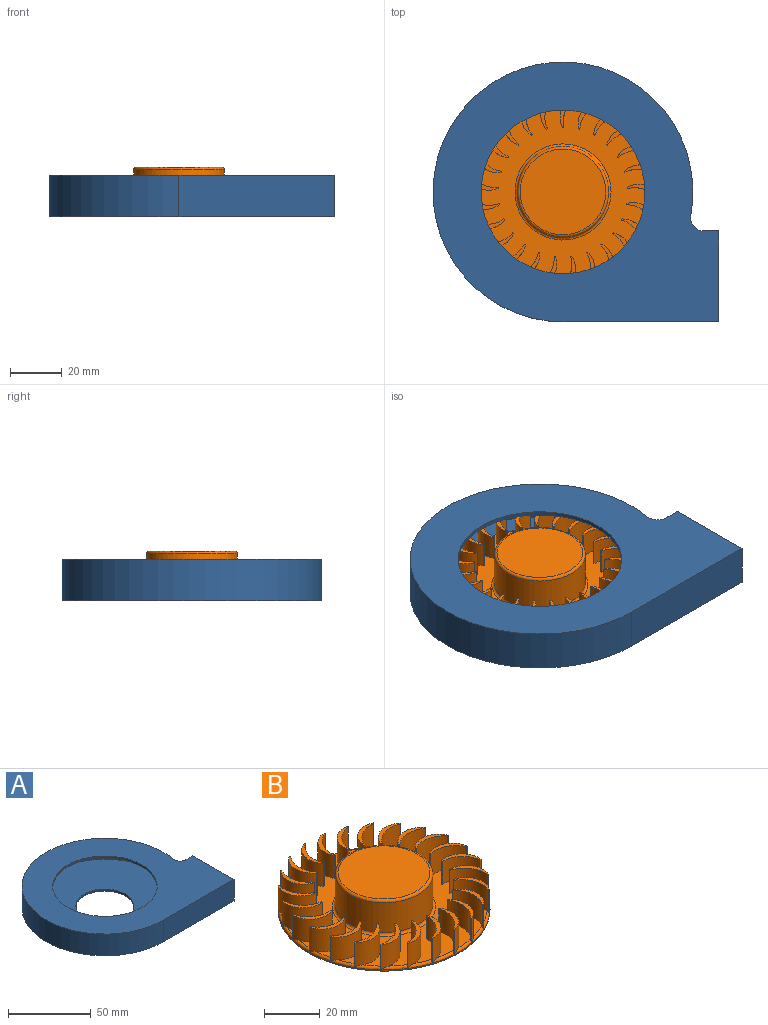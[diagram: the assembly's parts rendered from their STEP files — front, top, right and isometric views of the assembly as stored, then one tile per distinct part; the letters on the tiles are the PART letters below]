
ASSEMBLY  parts=2 mates=1
PART A: 15 faces, bbox 110x100x16 mm
  f0: cylinder r=17.5mm len=35mm, axis (0,0,-1), area 164.9mm2, adj f7,f13
  f1: plane 35x16mm, normal (1,0,0), area 144mm2, adj f2,f5,f6,f7,f8,f11,f12,f13
  f2: plane 16x5.92mm, normal (0,1,0), area 94.7mm2, adj f1,f3,f6,f7
  f3: cylinder r=5mm len=16mm, axis (0,0,-1), area 140.3mm2, adj f2,f4,f6,f7
  f4: cylinder r=50mm len=100mm, axis (0,0,-1), area 3916.2mm2, adj f3,f5,f6,f7
  f5: plane 60x16mm, normal (0,-1,0), area 960mm2, adj f1,f4,f6,f7
  f6: plane 110x100mm, normal (0,0,1), area 5620.7mm2, adj f1,f2,f3,f4,f5,f14
  f7: plane 110x100mm, normal (0,0,-1), area 7775.8mm2, adj f0,f1,f2,f3,f4,f5
  f8: plane 13x5.92mm, normal (0,-1,0), area 76.9mm2, adj f1,f9,f12,f13
  f9: cylinder r=6.5mm len=13mm, axis (0,0,-1), area 148.2mm2, adj f8,f10,f12,f13
  f10: cylinder r=48.5mm len=97mm, axis (0,0,-1), area 3086.4mm2, adj f9,f11,f12,f13
  f11: plane 60x13mm, normal (0,1,0), area 780mm2, adj f1,f10,f12,f13
  f12: plane 108.5x97mm, normal (0,0,-1), area 5145.1mm2, adj f1,f8,f9,f10,f11,f14
  f13: plane 108.5x97mm, normal (0,0,1), area 7300.2mm2, adj f0,f1,f8,f9,f10,f11
  f14: cylinder r=31.5mm len=63mm, axis (0,0,-1), area 296.9mm2, adj f6,f12
PART B: 160 faces, bbox 76.7x76.7x16.5 mm
  f0: torus R=37mm, axis (0,0,1), area 13.3mm2, adj f25,f27,f150,f153,f156
  f1: torus R=37mm, axis (0,0,1), area 13.3mm2, adj f25,f27,f145,f148,f151
  f2: torus R=37mm, axis (0,0,1), area 13.3mm2, adj f25,f27,f140,f143,f146
  f3: torus R=37mm, axis (0,0,1), area 13.3mm2, adj f25,f27,f135,f138,f141
  f4: torus R=37mm, axis (0,0,1), area 13.3mm2, adj f25,f27,f130,f133,f136
  f5: torus R=37mm, axis (0,0,1), area 13.3mm2, adj f25,f27,f125,f128,f131
  f6: torus R=37mm, axis (0,0,1), area 13.3mm2, adj f25,f27,f120,f123,f126
  f7: torus R=37mm, axis (0,0,1), area 13.3mm2, adj f25,f27,f115,f118,f121
  f8: torus R=37mm, axis (0,0,1), area 13.3mm2, adj f25,f27,f110,f113,f116
  f9: torus R=37mm, axis (0,0,1), area 13.3mm2, adj f25,f27,f105,f108,f111
  f10: torus R=37mm, axis (0,0,1), area 13.3mm2, adj f25,f27,f100,f103,f106
  f11: torus R=37mm, axis (0,0,1), area 13.3mm2, adj f25,f27,f95,f98,f101
  f12: torus R=37mm, axis (0,0,1), area 13.3mm2, adj f25,f27,f90,f93,f96
  f13: torus R=37mm, axis (0,0,1), area 13.3mm2, adj f25,f27,f85,f88,f91
  f14: torus R=37mm, axis (0,0,1), area 13.3mm2, adj f25,f27,f80,f83,f86
  f15: torus R=37mm, axis (0,0,1), area 13.3mm2, adj f25,f27,f75,f78,f81
  f16: torus R=37mm, axis (0,0,1), area 13.3mm2, adj f25,f27,f70,f73,f76
  f17: torus R=37mm, axis (0,0,1), area 13.3mm2, adj f25,f27,f65,f68,f71
  f18: torus R=37mm, axis (0,0,1), area 13.3mm2, adj f25,f27,f60,f63,f66
  f19: torus R=37mm, axis (0,0,1), area 13.3mm2, adj f25,f27,f55,f58,f61
  f20: torus R=37mm, axis (0,0,1), area 13.3mm2, adj f25,f27,f50,f53,f56
  f21: torus R=37mm, axis (0,0,1), area 13.3mm2, adj f25,f27,f45,f48,f51
  f22: torus R=37mm, axis (0,0,1), area 13.3mm2, adj f25,f27,f40,f43,f46
  f23: torus R=37mm, axis (0,0,1), area 13.3mm2, adj f25,f27,f35,f38,f41
  f24: torus R=37mm, axis (0,0,1), area 13.3mm2, adj f25,f27,f36,f155,f158
  f25: cylinder r=38mm len=76mm, axis (0,0,1), area 119.4mm2, adj f0,f1,f2,f3,f4,f5,f6,f7
  f26: plane 76x76mm, normal (0,0,-1), area 3461.2mm2, adj f25,f34
  f27: plane 74x74mm, normal (0,0,1), area 2753.3mm2, adj f0,f1,f2,f3,f4,f5,f6,f7
  f28: cylinder r=17.5mm len=35mm, axis (0,0,-1), area 1429.4mm2, adj f32,f33
  f29: plane 33x33mm, normal (0,0,1), area 855.3mm2, adj f33
  f30: cylinder r=16mm len=32mm, axis (0,0,-1), area 1256.6mm2, adj f31,f34
  f31: plane 32x32mm, normal (0,0,-1), area 804.2mm2, adj f30
  f32: torus R=18.5mm, axis (0,0,1), area 176.3mm2, adj f27,f28
  f33: torus R=16.5mm, axis (0,0,1), area 169.1mm2, adj f28,f29
  f34: torus R=18.5mm, axis (0,0,1), area 417.2mm2, adj f26,f30
  f35: plane 11x0.49mm, normal (0.98,-0.19,0), area 5.2mm2, adj f23,f36,f38,f39
  f36: cylinder r=8.55mm len=12.34mm, axis (0,0,-1), area 170.8mm2, adj f24,f27,f35,f37,f39
  f37: cylinder r=25mm len=10mm, axis (0,0,-1), area 5mm2, adj f27,f36,f38,f39
  f38: cylinder r=10.51mm len=11.85mm, axis (0,0,-1), area 148.2mm2, adj f23,f27,f35,f37,f39
  f39: plane 12.34x8.19mm, normal (0,0,1), area 20.2mm2, adj f35,f36,f37,f38
  f40: plane 11x0.45mm, normal (0.91,-0.42,0), area 5.2mm2, adj f22,f41,f43,f44
  f41: cylinder r=8.55mm len=11mm, axis (0,0,-1), area 170.8mm2, adj f23,f27,f40,f42,f44
  f42: cylinder r=25mm len=10mm, axis (0,0,-1), area 5mm2, adj f27,f41,f43,f44
  f43: cylinder r=10.51mm len=10.13mm, axis (0,0,-1), area 148.2mm2, adj f22,f27,f40,f42,f44
  f44: plane 10.45x10.32mm, normal (0,0,1), area 20.2mm2, adj f40,f41,f42,f43
  f45: plane 11x0.39mm, normal (0.77,-0.64,0), area 5.2mm2, adj f21,f46,f48,f49
  f46: cylinder r=8.55mm len=12.34mm, axis (0,0,-1), area 170.8mm2, adj f22,f27,f45,f47,f49
  f47: cylinder r=25mm len=10mm, axis (0,0,-1), area 5mm2, adj f27,f46,f48,f49
  f48: cylinder r=10.51mm len=11.58mm, axis (0,0,-1), area 148.2mm2, adj f21,f27,f45,f47,f49
  f49: plane 12.34x8.43mm, normal (0,0,1), area 20.2mm2, adj f45,f46,f47,f48
  f50: plane 11x0.4mm, normal (0.59,-0.81,0), area 5.2mm2, adj f20,f51,f53,f54
  f51: cylinder r=8.55mm len=13.77mm, axis (0,0,-1), area 170.8mm2, adj f21,f27,f50,f52,f54
  f52: cylinder r=25mm len=10mm, axis (0,0,-1), area 5mm2, adj f27,f51,f53,f54
  f53: cylinder r=10.51mm len=13mm, axis (0,0,-1), area 148.2mm2, adj f20,f27,f50,f52,f54
  f54: plane 13.77x6.42mm, normal (0,0,1), area 20.2mm2, adj f50,f51,f52,f53
  f55: plane 11x0.46mm, normal (0.37,-0.93,0), area 5.2mm2, adj f19,f56,f58,f59
  f56: cylinder r=8.55mm len=14.33mm, axis (0,0,-1), area 170.8mm2, adj f20,f27,f55,f57,f59
  f57: cylinder r=25mm len=10mm, axis (0,0,-1), area 5mm2, adj f27,f56,f58,f59
  f58: cylinder r=10.51mm len=13.6mm, axis (0,0,-1), area 148.2mm2, adj f19,f27,f55,f57,f59
  f59: plane 14.33x4.54mm, normal (0,0,1), area 20.2mm2, adj f55,f56,f57,f58
  f60: plane 11x0.5mm, normal (0.13,-0.99,0), area 5.2mm2, adj f18,f61,f63,f64
  f61: cylinder r=8.55mm len=13.99mm, axis (0,0,-1), area 170.8mm2, adj f19,f27,f60,f62,f64
  f62: cylinder r=25mm len=10mm, axis (0,0,-1), area 5mm2, adj f27,f61,f63,f64
  f63: cylinder r=10.51mm len=13.34mm, axis (0,0,-1), area 148.2mm2, adj f18,f27,f60,f62,f64
  f64: plane 13.99x5.63mm, normal (0,0,1), area 20.2mm2, adj f60,f61,f62,f63
  f65: plane 11x0.5mm, normal (-0.12,-0.99,0), area 5.2mm2, adj f17,f66,f68,f69
  f66: cylinder r=8.55mm len=12.78mm, axis (0,0,-1), area 170.8mm2, adj f18,f27,f65,f67,f69
  f67: cylinder r=25mm len=10mm, axis (0,0,-1), area 5mm2, adj f27,f66,f68,f69
  f68: cylinder r=10.51mm len=12.25mm, axis (0,0,-1), area 148.2mm2, adj f17,f27,f65,f67,f69
  f69: plane 12.78x7.65mm, normal (0,0,1), area 20.2mm2, adj f65,f66,f67,f68
  f70: plane 11x0.47mm, normal (-0.37,-0.93,0), area 5.2mm2, adj f16,f71,f73,f74
  f71: cylinder r=8.55mm len=11mm, axis (0,0,-1), area 170.8mm2, adj f17,f27,f70,f72,f74
  f72: cylinder r=25mm len=10mm, axis (0,0,-1), area 5mm2, adj f27,f71,f73,f74
  f73: cylinder r=10.51mm len=10.39mm, axis (0,0,-1), area 148.2mm2, adj f16,f27,f70,f72,f74
  f74: plane 10.94x9.8mm, normal (0,0,1), area 20.2mm2, adj f70,f71,f72,f73
  f75: plane 11x0.41mm, normal (-0.59,-0.81,0), area 5.2mm2, adj f15,f76,f78,f79
  f76: cylinder r=8.55mm len=11.86mm, axis (0,0,-1), area 170.8mm2, adj f16,f27,f75,f77,f79
  f77: cylinder r=25mm len=10mm, axis (0,0,-1), area 5mm2, adj f27,f76,f78,f79
  f78: cylinder r=10.51mm len=11.11mm, axis (0,0,-1), area 148.2mm2, adj f15,f27,f75,f77,f79
  f79: plane 11.86x8.94mm, normal (0,0,1), area 20.2mm2, adj f75,f76,f77,f78
  f80: plane 11x0.38mm, normal (-0.77,-0.64,0), area 5.2mm2, adj f14,f81,f83,f84
  f81: cylinder r=8.55mm len=13.49mm, axis (0,0,-1), area 170.8mm2, adj f15,f27,f80,f82,f84
  f82: cylinder r=25mm len=10mm, axis (0,0,-1), area 5mm2, adj f27,f81,f83,f84
  f83: cylinder r=10.51mm len=12.72mm, axis (0,0,-1), area 148.2mm2, adj f14,f27,f80,f82,f84
  f84: plane 13.49x6.92mm, normal (0,0,1), area 20.2mm2, adj f80,f81,f82,f83
  f85: plane 11x0.45mm, normal (-0.9,-0.43,0), area 5.2mm2, adj f13,f86,f88,f89
  f86: cylinder r=8.55mm len=14.27mm, axis (0,0,-1), area 170.8mm2, adj f14,f27,f85,f87,f89
  f87: cylinder r=25mm len=10mm, axis (0,0,-1), area 5mm2, adj f27,f86,f88,f89
  f88: cylinder r=10.51mm len=13.53mm, axis (0,0,-1), area 148.2mm2, adj f13,f27,f85,f87,f89
  f89: plane 14.27x4.99mm, normal (0,0,1), area 20.2mm2, adj f85,f86,f87,f88
  f90: plane 11x0.49mm, normal (-0.98,-0.19,0), area 5.2mm2, adj f12,f91,f93,f94
  f91: cylinder r=8.55mm len=14.16mm, axis (0,0,-1), area 170.8mm2, adj f13,f27,f90,f92,f94
  f92: cylinder r=25mm len=10mm, axis (0,0,-1), area 5mm2, adj f27,f91,f93,f94
  f93: cylinder r=10.51mm len=13.49mm, axis (0,0,-1), area 148.2mm2, adj f12,f27,f90,f92,f94
  f94: plane 14.16x5.17mm, normal (0,0,1), area 20.2mm2, adj f90,f91,f92,f93
  f95: plane 11x0.5mm, normal (-1,0.06,0), area 5.2mm2, adj f11,f96,f98,f99
  f96: cylinder r=8.55mm len=13.16mm, axis (0,0,-1), area 170.8mm2, adj f12,f27,f95,f97,f99
  f97: cylinder r=25mm len=10mm, axis (0,0,-1), area 5mm2, adj f27,f96,f98,f99
  f98: cylinder r=10.51mm len=12.6mm, axis (0,0,-1), area 148.2mm2, adj f11,f27,f95,f97,f99
  f99: plane 13.16x7.12mm, normal (0,0,1), area 20.2mm2, adj f95,f96,f97,f98
  f100: plane 11x0.48mm, normal (-0.95,0.31,0), area 5.2mm2, adj f10,f101,f103,f104
  f101: cylinder r=8.55mm len=11.36mm, axis (0,0,-1), area 170.8mm2, adj f11,f27,f100,f102,f104
  f102: cylinder r=25mm len=10mm, axis (0,0,-1), area 5mm2, adj f27,f101,f103,f104
  f103: cylinder r=10.51mm len=10.92mm, axis (0,0,-1), area 148.2mm2, adj f10,f27,f100,f102,f104
  f104: plane 11.42x9.26mm, normal (0,0,1), area 20.2mm2, adj f100,f101,f102,f103
  f105: plane 11x0.42mm, normal (-0.85,0.53,0), area 5.2mm2, adj f9,f106,f108,f109
  f106: cylinder r=8.55mm len=11.36mm, axis (0,0,-1), area 170.8mm2, adj f10,f27,f105,f107,f109
  f107: cylinder r=25mm len=10mm, axis (0,0,-1), area 5mm2, adj f27,f106,f108,f109
  f108: cylinder r=10.51mm len=10.6mm, axis (0,0,-1), area 148.2mm2, adj f9,f27,f105,f107,f109
  f109: plane 11.36x9.45mm, normal (0,0,1), area 20.2mm2, adj f105,f106,f107,f108
  f110: plane 11x0.36mm, normal (-0.69,0.73,0), area 5.2mm2, adj f8,f111,f113,f114
  f111: cylinder r=8.55mm len=13.16mm, axis (0,0,-1), area 170.8mm2, adj f9,f27,f110,f112,f114
  f112: cylinder r=25mm len=10mm, axis (0,0,-1), area 5mm2, adj f27,f111,f113,f114
  f113: cylinder r=10.51mm len=12.39mm, axis (0,0,-1), area 148.2mm2, adj f8,f27,f110,f112,f114
  f114: plane 13.16x7.42mm, normal (0,0,1), area 20.2mm2, adj f110,f111,f112,f113
  f115: plane 11x0.44mm, normal (-0.48,0.88,0), area 5.2mm2, adj f7,f116,f118,f119
  f116: cylinder r=8.55mm len=14.16mm, axis (0,0,-1), area 170.8mm2, adj f8,f27,f115,f117,f119
  f117: cylinder r=25mm len=10mm, axis (0,0,-1), area 5mm2, adj f27,f116,f118,f119
  f118: cylinder r=10.51mm len=13.4mm, axis (0,0,-1), area 148.2mm2, adj f7,f27,f115,f117,f119
  f119: plane 14.16x5.46mm, normal (0,0,1), area 20.2mm2, adj f115,f116,f117,f118
  f120: plane 11x0.48mm, normal (-0.25,0.97,0), area 5.2mm2, adj f6,f121,f123,f124
  f121: cylinder r=8.55mm len=14.27mm, axis (0,0,-1), area 170.8mm2, adj f7,f27,f120,f122,f124
  f122: cylinder r=25mm len=10mm, axis (0,0,-1), area 5mm2, adj f27,f121,f123,f124
  f123: cylinder r=10.51mm len=13.58mm, axis (0,0,-1), area 148.2mm2, adj f6,f27,f120,f122,f124
  f124: plane 14.27x4.71mm, normal (0,0,1), area 20.2mm2, adj f120,f121,f122,f123
  f125: plane 11x0.5mm, normal (0,1,0), area 5.2mm2, adj f5,f126,f128,f129
  f126: cylinder r=8.55mm len=13.49mm, axis (0,0,-1), area 170.8mm2, adj f6,f27,f125,f127,f129
  f127: cylinder r=25mm len=10mm, axis (0,0,-1), area 5mm2, adj f27,f126,f128,f129
  f128: cylinder r=10.51mm len=12.9mm, axis (0,0,-1), area 148.2mm2, adj f5,f27,f125,f127,f129
  f129: plane 13.49x6.6mm, normal (0,0,1), area 20.2mm2, adj f125,f126,f127,f128
  f130: plane 11x0.48mm, normal (0.25,0.97,0), area 5.2mm2, adj f4,f131,f133,f134
  f131: cylinder r=8.55mm len=11.86mm, axis (0,0,-1), area 170.8mm2, adj f5,f27,f130,f132,f134
  f132: cylinder r=25mm len=10mm, axis (0,0,-1), area 5mm2, adj f27,f131,f133,f134
  f133: cylinder r=10.51mm len=11.41mm, axis (0,0,-1), area 148.2mm2, adj f4,f27,f130,f132,f134
  f134: plane 11.89x8.73mm, normal (0,0,1), area 20.2mm2, adj f130,f131,f132,f133
  f135: plane 11x0.44mm, normal (0.48,0.88,0), area 5.2mm2, adj f3,f136,f138,f139
  f136: cylinder r=8.55mm len=11mm, axis (0,0,-1), area 170.8mm2, adj f4,f27,f135,f137,f139
  f137: cylinder r=25mm len=10mm, axis (0,0,-1), area 5mm2, adj f27,f136,f138,f139
  f138: cylinder r=10.51mm len=10.13mm, axis (0,0,-1), area 148.2mm2, adj f3,f27,f135,f137,f139
  f139: plane 10.85x9.95mm, normal (0,0,1), area 20.2mm2, adj f135,f136,f137,f138
  f140: plane 11x0.37mm, normal (0.68,0.73,0), area 5.2mm2, adj f2,f141,f143,f144
  f141: cylinder r=8.55mm len=12.77mm, axis (0,0,-1), area 170.8mm2, adj f3,f27,f140,f142,f144
  f142: cylinder r=25mm len=10mm, axis (0,0,-1), area 5mm2, adj f27,f141,f143,f144
  f143: cylinder r=10.51mm len=12.01mm, axis (0,0,-1), area 148.2mm2, adj f2,f27,f140,f142,f144
  f144: plane 12.77x7.92mm, normal (0,0,1), area 20.2mm2, adj f140,f141,f142,f143
  f145: plane 11x0.42mm, normal (0.84,0.54,0), area 5.2mm2, adj f1,f146,f148,f149
  f146: cylinder r=8.55mm len=13.99mm, axis (0,0,-1), area 170.8mm2, adj f2,f27,f145,f147,f149
  f147: cylinder r=25mm len=10mm, axis (0,0,-1), area 5mm2, adj f27,f146,f148,f149
  f148: cylinder r=10.51mm len=13.23mm, axis (0,0,-1), area 148.2mm2, adj f1,f27,f145,f147,f149
  f149: plane 13.99x5.94mm, normal (0,0,1), area 20.2mm2, adj f145,f146,f147,f148
  f150: plane 11x0.48mm, normal (0.95,0.31,0), area 5.2mm2, adj f0,f151,f153,f154
  f151: cylinder r=8.55mm len=14.33mm, axis (0,0,-1), area 170.8mm2, adj f1,f27,f150,f152,f154
  f152: cylinder r=25mm len=10mm, axis (0,0,-1), area 5mm2, adj f27,f151,f153,f154
  f153: cylinder r=10.51mm len=13.61mm, axis (0,0,-1), area 148.2mm2, adj f0,f27,f150,f152,f154
  f154: plane 14.33x4.28mm, normal (0,0,1), area 20.2mm2, adj f150,f151,f152,f153
  f155: plane 11x0.5mm, normal (1,0.06,0), area 5.2mm2, adj f24,f156,f158,f159
  f156: cylinder r=8.55mm len=13.77mm, axis (0,0,-1), area 170.8mm2, adj f0,f27,f155,f157,f159
  f157: cylinder r=25mm len=10mm, axis (0,0,-1), area 5mm2, adj f27,f156,f158,f159
  f158: cylinder r=10.51mm len=13.15mm, axis (0,0,-1), area 148.2mm2, adj f24,f27,f155,f157,f159
  f159: plane 13.77x6.11mm, normal (0,0,1), area 20.2mm2, adj f155,f156,f157,f158
PLACE A at identity fixed
PLACE B at identity
MATE revolute B.f0 <-> A.f0  axis (0,0,-1) through (0,0,-1.5)mm
